# Revit family: Drain_Floor_Parking Deck_15_Inch_Diameter_Zurn-Z537-Heavy-Duty-1
name_source: partatom
category: Plumbing Fixtures
units: mm (PartAtom-declared; Revit-internal decimal feet)

## family parameters
Always vertical = Yes
Cut with Voids When Loaded = No
Maintain Annotation Orientation = No
OmniClass Number = 23.70.50.21.24.14
OmniClass Title = Deck Waste Water Drains
Part Type = Normal
Room Calculation Point = No
Round Connector Dimension = Use Radius
Shared = No
Work Plane-Based = No

## types (1)
- Load Family Type Catalog
    Approx. Wt. Lbs. = 122 "
    Assembly Code = D2030300
    Body Height_E = 4.625 "
    CW Connection = No
    CWFU = 1
    Connector Radius = 1 "
    Default Elevation = 0 "
    Description = 15-7/8 [403] SQUARE TOP HEAVY-DUTY PARKING DECK DRAIN W/ SUPPORT FLANGE
    Frame & Grate = Iron - Zurn -Cast - Painted - Blue
    Frame Height = 1.5 "
    Grate Open Area Sq.in = 79 "
    HW Connection = No
    HWFU = 1
    Main Material = Iron - Zurn -Cast - Painted - Blue
    Manufacturer = Zurn Water, LLC
    Manufacturer Brand = Zurn
    Model = Z537
    Modified Date = 11/28/2025
    Pipe Size_A Inside Diameter = 2.067 "
    Pipe Size_A Nominal Diameter = 2 "
    Pipe Size_A Outer Diameter = 2.375 "
    Product Documentation Link = https://files.zurn.com
    Product Page URL = https://www.zurn.com
    Product data URL = https://www.bimobject.com
    Top Diameter = 15.875 "
    Type Comments = Z537-2 Inch Neo-Loc Outlet
    URL = www.zurn.com
    Vent Connection = No
    WFU = 0
    Waste Connection = Yes
    Width = 24 "
    ZN Height Difference = 0.188 "

## geometry (parser evidence)
native form markers: Sweep x3
no freeform markers — native parametric forms only
